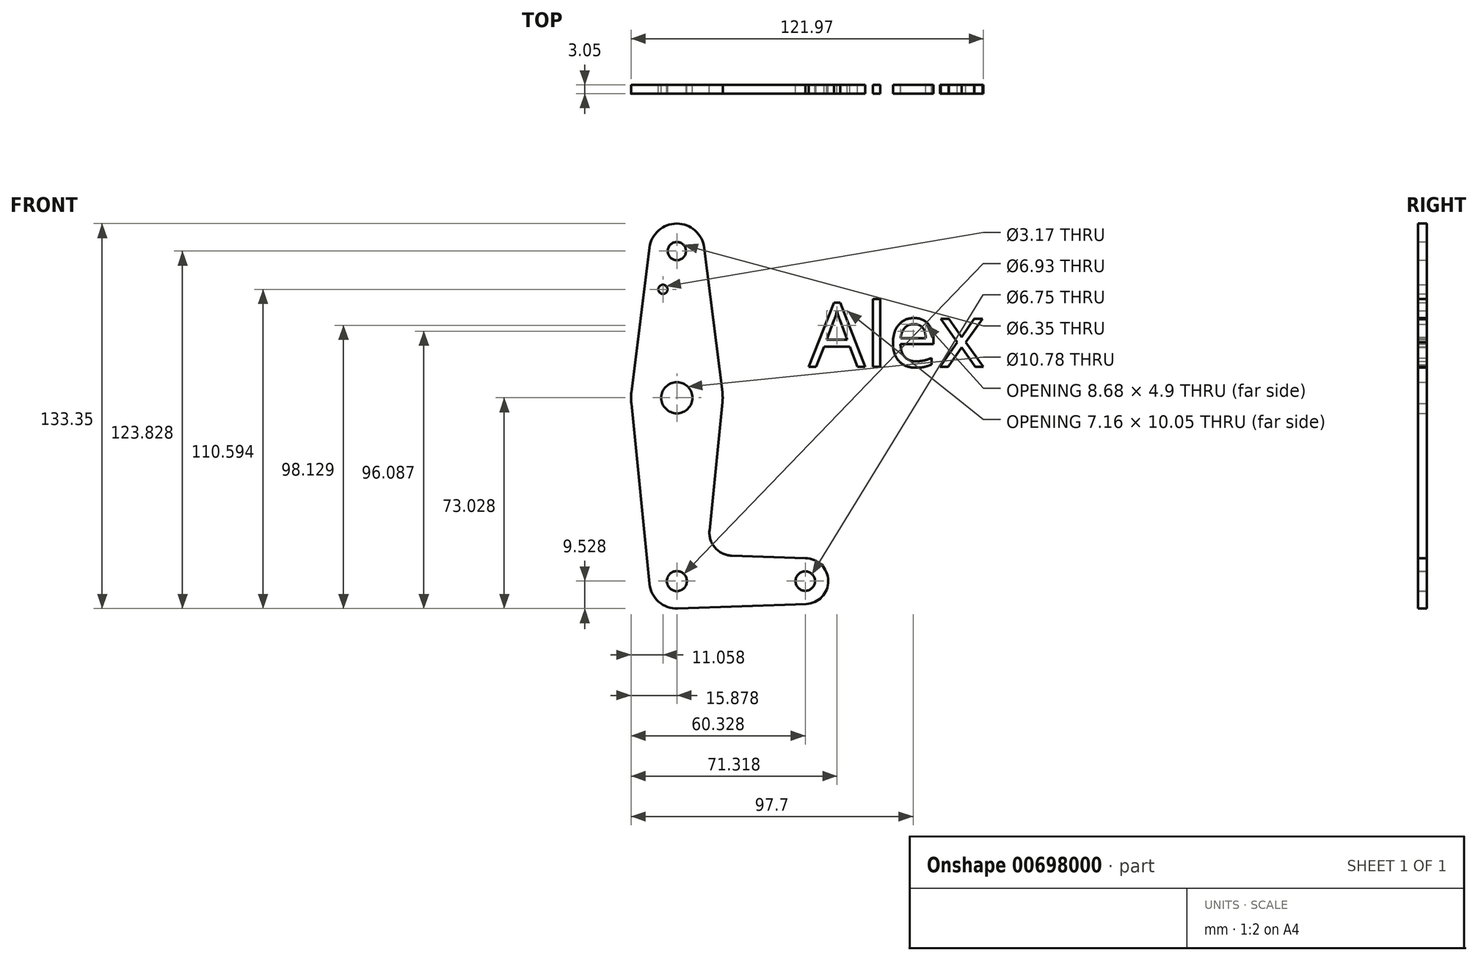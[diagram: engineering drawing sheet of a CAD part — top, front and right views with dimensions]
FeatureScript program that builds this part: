
annotation { "Feature Type Name" : "Feature", "Feature Type Description" : "" }
export const myFeature = defineFeature(function(context is Context, id is Id, definition is map)
    precondition{}
    {
        {
            var Q0;
            Q0=qCreatedBy(makeId("Front.planeOp"),FACE);
            var sketch = newSketch(context, id + "F0", { "sketchPlane" : qUnion([Q0])});
            skLineSegment(sketch, "E0", {"start": v(-27.61, 90.33) * mm, "end": v(-27.61, -23.97) * mm, "construction": true});
            skLineSegment(sketch, "E1", {"start": v(-27.61, -23.97) * mm, "end": v(16.84, -23.97) * mm, "construction": true});
            skCircle(sketch, "E2", {"center": v(-27.61, -23.97) * mm, "radius": 9.53 * mm});
            skCircle(sketch, "E3", {"center": v(-27.61, 39.53) * mm, "radius": 15.88 * mm});
            skCircle(sketch, "E4", {"center": v(-27.61, 90.33) * mm, "radius": 9.53 * mm});
            skCircle(sketch, "E5", {"center": v(16.84, -23.97) * mm, "radius": 7.94 * mm});
            skLineSegment(sketch, "E6", {"start": v(-43.44, 38.32) * mm, "end": v(-37.09, -24.92) * mm});
            skLineSegment(sketch, "E7", {"start": v(-27.5, -33.5) * mm, "end": v(-27.04, -33.48) * mm});
            skLineSegment(sketch, "E8", {"start": v(16.9, -16.04) * mm, "end": v(-8.68, -15.12) * mm});
            skLineSegment(sketch, "E9", {"start": v(-16.3, -6.38) * mm, "end": v(-11.82, 37.93) * mm});
            skLineSegment(sketch, "E10", {"start": v(-37.06, 91.52) * mm, "end": v(-43.36, 41.51) * mm});
            skLineSegment(sketch, "E11", {"start": v(-18.16, 91.52) * mm, "end": v(-11.86, 41.51) * mm});
            skCircle(sketch, "E12", {"center": v(-27.61, 90.33) * mm, "radius": 3.18 * mm});
            skCircle(sketch, "E13", {"center": v(-32.43, 77.1) * mm, "radius": 1.59 * mm});
            skCircle(sketch, "E14", {"center": v(-27.61, 39.53) * mm, "radius": 5.39 * mm});
            skCircle(sketch, "E15", {"center": v(-27.61, -23.97) * mm, "radius": 3.46 * mm});
            skCircle(sketch, "E16", {"center": v(16.84, -23.97) * mm, "radius": 3.37 * mm});
            skArc(sketch, "E17.filletArc", {"start": v(-16.3, -6.38) * mm, "mid": v(-14.39, -12.4) * mm, "end": v(-8.68, -15.12) * mm});
            skPoint(sketch, "E18.orphan", {"position": v(16.84, -31.91) * mm});
            skLineSegment(sketch, "E19", {"start": v(-27.27, -33.5) * mm, "end": v(17.12, -31.9) * mm});
            skText(sketch, "E20", { "text": "Alex", "fontName": "OpenSans-Regular.ttf"});
            const initialGuessF0  = {"E20": [0.01801, 0.05025, 1, 0, 0.02232]};
            skSetInitialGuess(sketch, initialGuessF0);
            skSolve(sketch);
        }
        {
            var Q0;
            Q0 = qSketchRegion(id + "F0", true);
            extrude(context, id + "F1", {"entities" : qUnion([Q0]), "depth" : 3.05 * mm, "offsetDistance" : 25.4 * mm});
        }
    });
